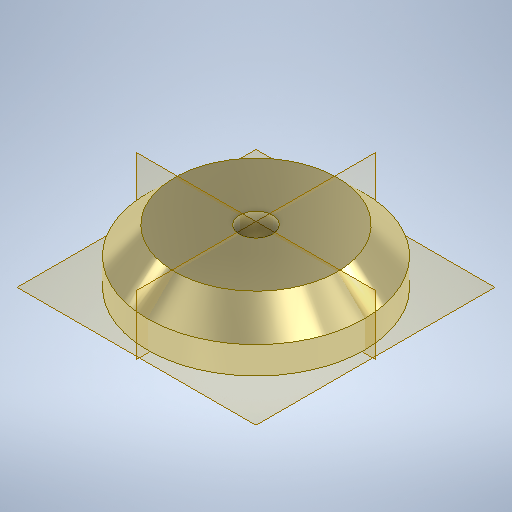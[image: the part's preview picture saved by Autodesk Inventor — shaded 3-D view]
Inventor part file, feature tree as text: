
AUTODESK INVENTOR PART (.ipt)
format: ipt  version: 2025.2 (Build 292293000, 293)  size: 267,264 bytes
history: native  units: mm
features: sketch x3, other x2, extrude x2
ambient origin geometry x8: Origin, YZ Plane, XZ Plane, XY Plane, X Axis, Y Axis, Z Axis, Center Point
bodies: Body1 (feature_tree)
feature tree (7):
  other  "Sólido1"
  other  "Revolução1"
  extrude  "Extrusão1"  Depth=10.0mm
  extrude  "Extrusão2"  Depth=30.0mm
  sketch  "Esboço1"  dims[d0=40.0mm d1=10.0mm]
  sketch  "Esboço2"  dims[d6=135.0deg d7=30.0mm]
  sketch  "Esboço3"  dims[d8=360.0deg d9=12.2mm d10=10.0mm d11=0.0mm d12=10.0mm d13=10.0mm d14=0.0mm]
